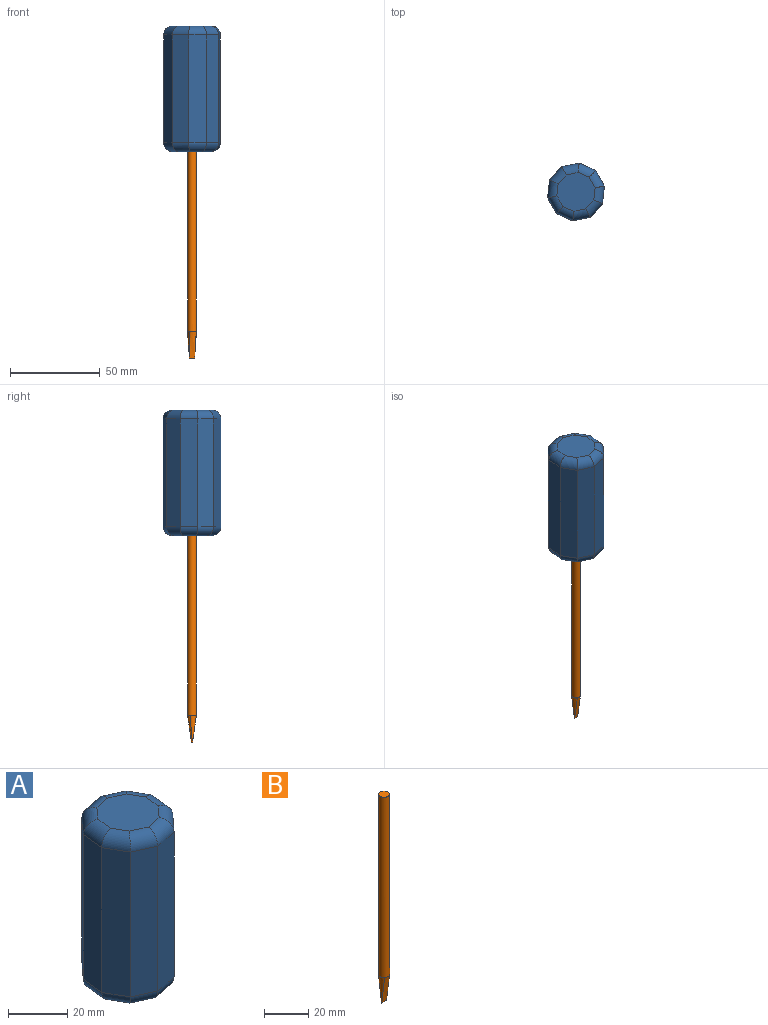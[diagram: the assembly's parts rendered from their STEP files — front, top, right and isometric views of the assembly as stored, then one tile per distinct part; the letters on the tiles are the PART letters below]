
ASSEMBLY  parts=2 mates=1
PART A: 32 faces, bbox 31.6x32.1x70 mm
  f0: plane 60x7.39mm, normal (0.74,-0.67,0), area 599.3mm2, adj f1,f9,f18,f28
  f1: plane 60x9.93mm, normal (0.99,-0.11,0), area 599.3mm2, adj f0,f2,f16,f26
  f2: plane 60x8.67mm, normal (0.87,0.5,0), area 599.3mm2, adj f1,f3,f14,f24
  f3: plane 60x9.11mm, normal (0.41,0.91,0), area 599.3mm2, adj f2,f4,f12,f22
  f4: plane 60x9.78mm, normal (-0.2,0.98,0), area 599.3mm2, adj f3,f5,f13,f23
  f5: plane 60x7.39mm, normal (-0.74,0.67,0), area 599.3mm2, adj f4,f6,f15,f25
  f6: plane 60x9.93mm, normal (-0.99,0.11,0), area 599.3mm2, adj f5,f7,f17,f27
  f7: plane 60x8.67mm, normal (-0.87,-0.5,0), area 599.3mm2, adj f6,f8,f19,f29
  f8: plane 60x9.11mm, normal (-0.41,-0.91,0), area 599.3mm2, adj f7,f9,f21,f31
  f9: plane 60x9.78mm, normal (0.2,-0.98,0), area 599.3mm2, adj f0,f8,f20,f30
  f10: plane 21.68x21.35mm, normal (0,0,1), area 349.4mm2, adj f22,f23,f24,f25,f26,f27,f28,f29
  f11: plane 21.68x21.35mm, normal (0,0,-1), area 349.4mm2, adj f12,f13,f14,f15,f16,f17,f18,f19
  f12: cylinder r=5mm len=11.16mm, axis (-0.91,0.41,0), area 69.2mm2, adj f3,f11,f13,f14
  f13: cylinder r=5mm len=10.8mm, axis (-0.98,-0.2,0), area 69.2mm2, adj f4,f11,f12,f15
  f14: cylinder r=5mm len=11.15mm, axis (-0.5,0.87,0), area 69.2mm2, adj f2,f11,f12,f16
  f15: cylinder r=5mm len=10.75mm, axis (-0.67,-0.74,0), area 69.2mm2, adj f5,f11,f13,f17
  f16: cylinder r=5mm len=10.47mm, axis (0.11,0.99,0), area 69.2mm2, adj f1,f11,f14,f18
  f17: cylinder r=5mm len=10.47mm, axis (-0.11,-0.99,0), area 69.2mm2, adj f6,f11,f15,f19
  f18: cylinder r=5mm len=10.75mm, axis (0.67,0.74,0), area 69.2mm2, adj f0,f11,f16,f20
  f19: cylinder r=5mm len=11.15mm, axis (0.5,-0.87,0), area 69.2mm2, adj f7,f11,f17,f21
  f20: cylinder r=5mm len=10.8mm, axis (0.98,0.2,0), area 69.2mm2, adj f9,f11,f18,f21
  f21: cylinder r=5mm len=11.16mm, axis (0.91,-0.41,0), area 69.2mm2, adj f8,f11,f19,f20
  f22: cylinder r=5mm len=11.16mm, axis (0.91,-0.41,0), area 69.2mm2, adj f3,f10,f23,f24
  f23: cylinder r=5mm len=10.8mm, axis (0.98,0.2,0), area 69.2mm2, adj f4,f10,f22,f25
  f24: cylinder r=5mm len=11.15mm, axis (0.5,-0.87,0), area 69.2mm2, adj f2,f10,f22,f26
  f25: cylinder r=5mm len=10.75mm, axis (0.67,0.74,0), area 69.2mm2, adj f5,f10,f23,f27
  f26: cylinder r=5mm len=10.47mm, axis (-0.11,-0.99,0), area 69.2mm2, adj f1,f10,f24,f28
  f27: cylinder r=5mm len=10.47mm, axis (0.11,0.99,0), area 69.2mm2, adj f6,f10,f25,f29
  f28: cylinder r=5mm len=10.75mm, axis (-0.67,-0.74,0), area 69.2mm2, adj f0,f10,f26,f30
  f29: cylinder r=5mm len=11.15mm, axis (-0.5,0.87,0), area 69.2mm2, adj f7,f10,f27,f31
  f30: cylinder r=5mm len=10.8mm, axis (-0.98,-0.2,0), area 69.2mm2, adj f9,f10,f28,f31
  f31: cylinder r=5mm len=11.16mm, axis (-0.91,0.41,0), area 69.2mm2, adj f8,f10,f29,f30
PART B: 7 faces, bbox 5x5x115 mm
  f0: cylinder r=2.5mm len=100mm, axis (0,0,1), area 1570.8mm2, adj f1,f3,f4,f5,f6
  f1: plane 5x5mm, normal (0,0,1), area 19.6mm2, adj f0
  f2: plane 3x0.2mm, normal (0,0,-1), area 0.6mm2, adj f3,f4,f5,f6
  f3: bspline ~15x3.52mm, area 51.6mm2, adj f0,f2,f4,f6
  f4: bspline ~15x3.52mm, area 30.9mm2, adj f0,f2,f3,f5
  f5: bspline ~15x3.52mm, area 51.6mm2, adj f0,f2,f4,f6
  f6: bspline ~15x3.52mm, area 30.9mm2, adj f0,f2,f3,f5
PLACE A at identity fixed
PLACE B rot(axis=(0,0,1),11.7deg) t=(0,0,0)mm
MATE revolute B.f0 <-> A.f11  axis (0,0,1) through (0,0,0)mm
